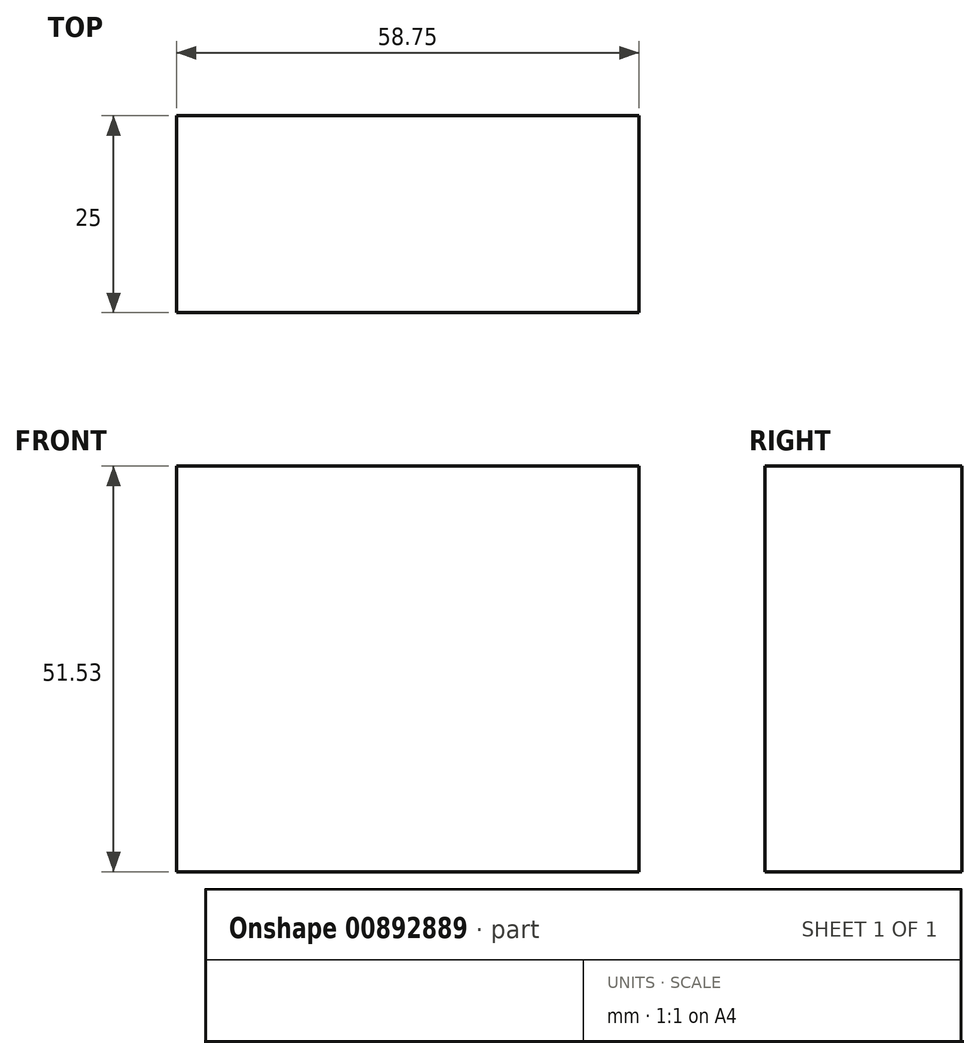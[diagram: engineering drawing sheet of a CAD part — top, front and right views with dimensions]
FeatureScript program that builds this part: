
annotation { "Feature Type Name" : "Feature", "Feature Type Description" : "" }
export const myFeature = defineFeature(function(context is Context, id is Id, definition is map)
    precondition{}
    {
        {
            var Q0;
            Q0=qCreatedBy(makeId("Front.planeOp"),FACE);
            var sketch = newSketch(context, id + "F0", { "sketchPlane" : qUnion([Q0])});
            skLineSegment(sketch, "E0.bottom", {"start": v(-120.25, 44.32) * mm, "end": v(-61.5, 44.32) * mm});
            skLineSegment(sketch, "E0.top", {"start": v(-120.25, -7.2) * mm, "end": v(-61.5, -7.2) * mm});
            skLineSegment(sketch, "E0.left", {"start": v(-120.25, 44.32) * mm, "end": v(-120.25, -7.2) * mm});
            skLineSegment(sketch, "E0.right", {"start": v(-61.5, 44.32) * mm, "end": v(-61.5, -7.2) * mm});
            skSolve(sketch);
        }
        {
            var Q0;
            Q0=makeQuery(id+"F0.imprint","IMPRINT",FACE,{"disambiguationData":[TD([[makeQuery(id+"F0.imprint","IMPRINT",EDGE,{"derivedFrom":sQuery(id+"F0.wireOp",EDGE,"E0.bottom")}),-1.0]])]});
            extrude(context, id + "F1", {"entities" : qUnion([Q0]), "depth" : 25 * mm, "offsetDistance" : 25 * mm});
        }
    });
